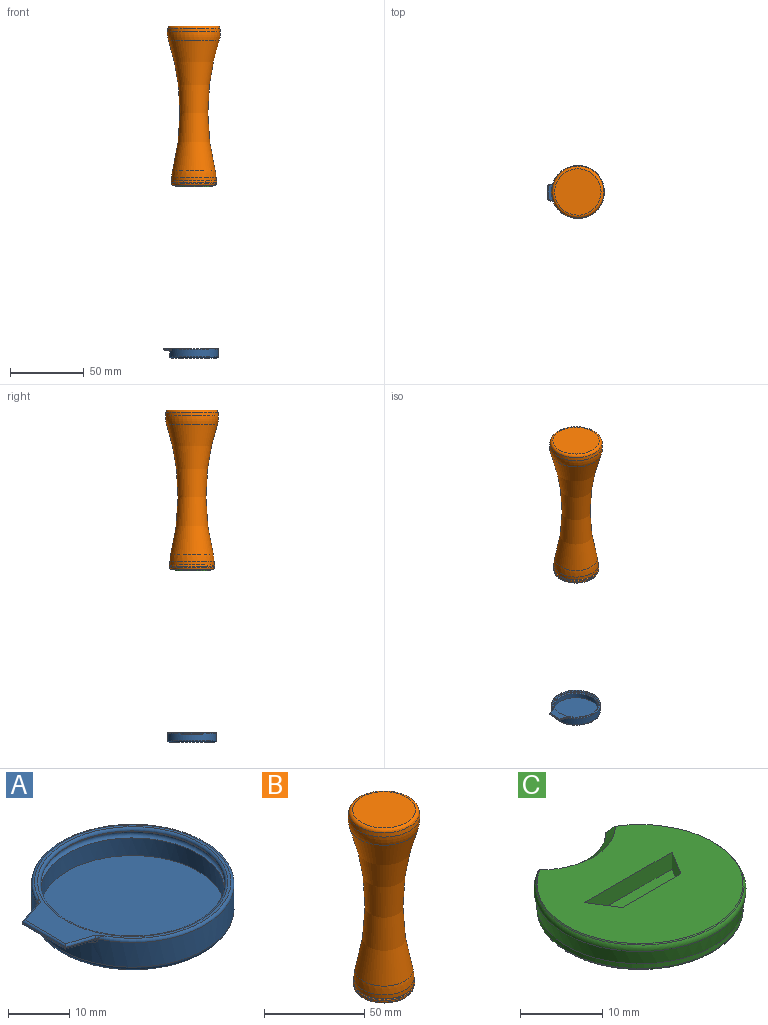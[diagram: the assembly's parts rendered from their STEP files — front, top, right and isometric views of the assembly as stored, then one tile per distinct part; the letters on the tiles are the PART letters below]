
ASSEMBLY  parts=3 mates=2
PART A: 29 faces, bbox 38.7x36.1x7.3 mm
  f0: cylinder r=16.5mm len=33mm, axis (0,0,-1), area 494.9mm2, adj f8,f9,f18,f20,f22
  f1: cylinder r=15mm len=30mm, axis (0,0,-1), area 329.9mm2, adj f5,f6
  f2: cylinder r=15mm len=30mm, axis (0,0,-1), area 6.6mm2, adj f7,f11
  f3: plane 36.48x32.38mm, normal (0,0,1), area 99mm2, adj f7,f8,f24,f25,f26,f27,f28
  f4: plane 31x31mm, normal (0,0,-1), area 754.8mm2, adj f9
  f5: torus R=15mm, axis (0,0,-1), area 174mm2, adj f1,f10
  f6: plane 30x30mm, normal (0,0,1), area 706.9mm2, adj f1
  f7: torus R=15.5mm, axis (0,0,-1), area 74.9mm2, adj f2,f3
  f8: torus R=16mm, axis (0,0,-1), area 68.6mm2, adj f0,f3,f16,f23
  f9: torus R=15.5mm, axis (0,0,-1), area 159.3mm2, adj f0,f4
  f10: cone r=15mm half-angle=40.9deg, axis (0,0,-1), area 8.9mm2, adj f5,f11
  f11: torus R=15.1mm, axis (0,0,1), area 6.7mm2, adj f2,f10
  f12: plane 10x0.1mm, normal (-1,0,0), area 1mm2, adj f13,f14,f19,f26
  f13: plane 5.26x1.72mm, normal (-0.31,-0.95,0), area 0.6mm2, adj f12,f21,f23,f25
  f14: plane 5.26x1.72mm, normal (-0.31,0.95,0), area 0.6mm2, adj f12,f16,f17,f27
  f15: plane 11.95x4.08mm, normal (0,0,-1), area 34.6mm2, adj f17,f19,f20,f21
  f16: bspline ~1.62x1.05mm, area 0.1mm2, adj f8,f14,f18,f28
  f17: cylinder r=0.5mm len=5.41mm, axis (0.95,0.31,0), area 3.9mm2, adj f14,f15,f18,f19
  f18: bspline ~1.49x1.15mm, area 0.8mm2, adj f0,f16,f17,f20
  f19: cylinder r=0.5mm len=10mm, axis (0,1,0), area 7.6mm2, adj f12,f15,f17,f21
  f20: torus R=17mm, axis (0,0,1), area 9.4mm2, adj f0,f15,f18,f22
  f21: cylinder r=0.5mm len=5.41mm, axis (-0.95,0.31,0), area 3.9mm2, adj f13,f15,f19,f22
  f22: bspline ~1.36x1.18mm, area 0.8mm2, adj f0,f20,f21,f23
  f23: bspline ~1.62x1.05mm, area 0.1mm2, adj f8,f13,f22,f24
  f24: bspline ~1.29x1.18mm, area 0.3mm2, adj f3,f23,f25
  f25: cylinder r=0.4mm len=5.38mm, axis (-0.95,0.31,0), area 3.4mm2, adj f3,f13,f24,f26
  f26: cylinder r=0.4mm len=10mm, axis (0,1,0), area 6.1mm2, adj f3,f12,f25,f27
  f27: cylinder r=0.4mm len=5.38mm, axis (0.95,0.31,0), area 3.4mm2, adj f3,f14,f26,f28
  f28: bspline ~1.29x1.18mm, area 0.3mm2, adj f3,f16,f27
PART B: 24 faces, bbox 119.4x119.4x224 mm
  f0: plane 31.35x31.35mm, normal (0,0,1), area 772mm2, adj f4
  f1: sphere r=17.96mm, area 264.9mm2, adj f4,f23
  f2: torus R=167.17mm, axis (0,0,-1), area 6519.8mm2, adj f5,f23
  f3: cylinder r=15mm len=30mm, axis (0,0,-1), area 226.1mm2, adj f5,f6
  f4: torus R=15.68mm, axis (0,0,1), area 292.6mm2, adj f0,f1
  f5: revolved ~30x30mm, area 933.3mm2, adj f2,f3
  f6: torus R=15mm, axis (0,0,-1), area 14.3mm2, adj f3,f13
  f7: plane 26x26mm, normal (0,0,-1), area 488.9mm2, adj f8,f14,f15,f16,f17
  f8: cone r=12.5mm half-angle=9.5deg, axis (0,0,1), area 243.6mm2, adj f7,f9
  f9: plane 28x28mm, normal (0,0,-1), area 124.9mm2, adj f8,f10
  f10: torus R=14mm, axis (0,0,1), area 144.5mm2, adj f9,f11
  f11: cylinder r=15mm len=30mm, axis (0,0,-1), area 94.2mm2, adj f10,f12
  f12: cone r=15mm half-angle=45deg, axis (0,0,1), area 42.1mm2, adj f11,f13
  f13: torus R=15.03mm, axis (0,0,1), area 79.3mm2, adj f6,f12
  f14: plane 3.5x2.5mm, normal (0.81,-0.58,0), area 4.3mm2, adj f7,f15,f17,f19
  f15: plane 9.5x1mm, normal (0,-1,0), area 9.5mm2, adj f7,f14,f16,f21
  f16: plane 3.5x2.5mm, normal (-0.81,-0.58,0), area 4.3mm2, adj f7,f15,f17,f22
  f17: plane 14.5x1mm, normal (0,1,0), area 14.5mm2, adj f7,f14,f16,f20
  f18: plane 12.56x2.5mm, normal (0,0,-1), area 26.9mm2, adj f19,f20,f21,f22
  f19: cylinder r=0.5mm len=3.79mm, axis (0.58,0.81,0), area 3mm2, adj f14,f18,f20,f21
  f20: cylinder r=0.5mm len=14.5mm, axis (-1,0,0), area 10.8mm2, adj f17,f18,f19,f22
  f21: cylinder r=0.5mm len=9.5mm, axis (1,0,0), area 7.3mm2, adj f15,f18,f19,f22
  f22: cylinder r=0.5mm len=3.79mm, axis (0.58,-0.81,0), area 3mm2, adj f16,f18,f20,f21
  f23: torus R=2.96mm, axis (0,0,1), area 623.5mm2, adj f1,f2
PART C: 44 faces, bbox 27.8x26.4x4 mm
  f0: plane 25x23.19mm, normal (0,0,1), area 401mm2, adj f3,f4,f5,f6,f31,f43
  f1: plane 23.4x22.55mm, normal (0,0,-1), area 386.4mm2, adj f8,f9,f10,f11,f12,f13,f14,f15
  f2: cone r=13mm half-angle=9.5deg, axis (0,0,1), area 142.3mm2, adj f32,f33,f37,f43
  f3: plane 4x2.5mm, normal (0.85,0.53,0), area 11.8mm2, adj f0,f4,f6,f7
  f4: plane 10x2.5mm, normal (0,1,0), area 25mm2, adj f0,f3,f5,f7
  f5: plane 4x2.5mm, normal (-0.85,0.53,0), area 11.8mm2, adj f0,f4,f6,f7
  f6: plane 15x2.5mm, normal (0,-1,0), area 37.5mm2, adj f0,f3,f5,f7
  f7: plane 15x4mm, normal (0,0,1), area 50mm2, adj f3,f4,f5,f6
  f8: plane 1.61x1mm, normal (0,1,0), area 1.6mm2, adj f1,f19,f20,f30
  f9: plane 1.05x1mm, normal (-1,0,0), area 1.1mm2, adj f1,f19,f20,f21
  f10: plane 5.58x1mm, normal (0,-1,0), area 5.6mm2, adj f1,f19,f21,f22
  f11: plane 1.05x1mm, normal (1,0,0), area 1.1mm2, adj f1,f19,f22,f23
  f12: plane 1.33x1mm, normal (0,1,0), area 1.3mm2, adj f1,f19,f23,f24
  f13: plane 8.02x1mm, normal (1,0,0), area 8mm2, adj f1,f19,f24,f25
  f14: plane 1.13x1mm, normal (0,1,0), area 1.1mm2, adj f1,f19,f25,f26
  f15: extruded ~2.08x1mm, area 2.2mm2, adj f1,f19,f26,f27
  f16: plane 1x0.72mm, normal (-1,0,0), area 0.7mm2, adj f1,f19,f27,f28
  f17: plane 1.26x1mm, normal (0,-1,0), area 1.3mm2, adj f1,f19,f28,f29
  f18: plane 5.9x1mm, normal (-1,0,0), area 5.9mm2, adj f1,f19,f29,f30
  f19: plane 10.28x6.18mm, normal (0,0,-1), area 30.5mm2, adj f8,f9,f10,f11,f12,f13,f14,f15
  f20: cylinder r=0.3mm len=1mm, axis (0,0,1), area 0.5mm2, adj f1,f8,f9,f19
  f21: cylinder r=0.3mm len=1mm, axis (0,0,1), area 0.5mm2, adj f1,f9,f10,f19
  f22: cylinder r=0.3mm len=1mm, axis (0,0,1), area 0.5mm2, adj f1,f10,f11,f19
  f23: cylinder r=0.3mm len=1mm, axis (0,0,1), area 0.5mm2, adj f1,f11,f12,f19
  f24: cylinder r=0.3mm len=1mm, axis (0,0,-1), area 0.5mm2, adj f1,f12,f13,f19
  f25: cylinder r=0.3mm len=1mm, axis (0,0,1), area 0.5mm2, adj f1,f13,f14,f19
  f26: cylinder r=0.3mm len=1mm, axis (0,0,1), area 0.2mm2, adj f1,f14,f15,f19
  f27: cylinder r=0.3mm len=1mm, axis (0,0,1), area 0.4mm2, adj f1,f15,f16,f19
  f28: cylinder r=0.3mm len=1mm, axis (0,0,1), area 0.5mm2, adj f1,f16,f17,f19
  f29: cylinder r=0.3mm len=1mm, axis (0,0,-1), area 0.5mm2, adj f1,f17,f18,f19
  f30: cylinder r=0.3mm len=1mm, axis (0,0,-1), area 0.5mm2, adj f1,f8,f18,f19
  f31: cone r=12.92mm half-angle=40.3deg, axis (0,0,-1), area 12mm2, adj f0,f32,f43
  f32: torus R=11.86mm, axis (0,0,1), area 58.7mm2, adj f2,f31,f43
  f33: cone r=8.12mm half-angle=9deg, axis (0,0,1), area 24.2mm2, adj f1,f2,f34,f36,f43
  f34: cylinder r=7.65mm len=0.72mm, axis (0,0,1), area 0.6mm2, adj f33,f35,f37,f39
  f35: cylinder r=11.7mm len=23.4mm, axis (0,0,1), area 45.2mm2, adj f1,f34,f36,f41
  f36: cylinder r=7.65mm len=0.72mm, axis (0,0,1), area 0.6mm2, adj f33,f35,f37,f42
  f37: cylinder r=12.5mm len=25mm, axis (0,0,1), area 47.6mm2, adj f2,f34,f36,f40
  f38: plane 24.4x23.26mm, normal (0,0,-1), area 13.1mm2, adj f39,f40,f41,f42
  f39: torus R=7.95mm, axis (0,0,-1), area 0.3mm2, adj f34,f38,f40,f41
  f40: torus R=12.2mm, axis (0,0,-1), area 31.7mm2, adj f37,f38,f39,f42
  f41: torus R=12mm, axis (0,0,-1), area 30.5mm2, adj f35,f38,f39,f42
  f42: torus R=7.95mm, axis (0,0,-1), area 0.3mm2, adj f36,f38,f40,f41
  f43: cone r=7.97mm half-angle=49.5deg, axis (0,0,1), area 20.8mm2, adj f0,f2,f31,f32,f33
PLACE A t=(0,-0.01,-171.56)mm
PLACE B t=(0,0,-31.64)mm
PLACE C t=(0,0,-54.64)mm
MATE slider B.f7 <-> A.f0  axis (0,0,-1) through (0,-0.01,-51.64)mm
MATE slider B.f2 <-> C.f2  axis (0,0,-1) through (0,0,-51.64)mm
